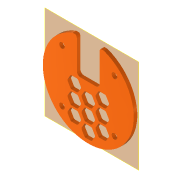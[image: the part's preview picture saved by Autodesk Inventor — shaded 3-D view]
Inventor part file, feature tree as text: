
AUTODESK INVENTOR PART (.ipt)
format: ipt  version: 2022 (Build 260153000, 153)  size: 285,696 bytes
history: native  units: mm
features: reference x6, extrude x3, sketch x3, plane x2, projected_geometry x2, other x2, hole x1, fillet x1, pattern_linear x1
ambient origin geometry x8: Origin, YZ Plane, XZ Plane, XY Plane, X Axis, Y Axis, Z Axis, Center Point
bodies: Volumenkörper1 (feature_tree)
feature tree (21):
  plane  "Arbeitsebene1"
  extrude  "Extrusion1"  Depth=4.0mm
  plane  "Arbeitsebene2"
  hole  "Bohrung1"  [1 undecoded]
  extrude  "Extrusion2"  Depth=2.0mm
  fillet  "Rundung1"  Radius=4.0mm
  extrude  "Extrusion3"  TaperAngle=0.0deg  [1 undecoded]
  pattern_linear  "Rechteckige Anordnung1"  Count1=3 Spacing1=8.0mm
  sketch  "Skizze1"  dims[d0=4.0mm d1=4.0mm]
  reference  "Referenz1"
  sketch  "Skizze2"  dims[d2=2.0mm d3=0.0mm]
  projected_geometry  "Projizierte Kontur1"
  reference  "Referenz2"
  reference  "Referenz3"
  reference  "Referenz4"
  reference  "Referenz5"
  reference  "Referenz6"
  sketch  "Skizze4"  dims[d4=3.2mm d5=6.0mm d6=4.0mm d7=2.0mm d8=90.0deg d9=8.0mm d10=20.594885mm d11=10.0mm d12=0.0mm d13=2.0mm d23=7.0mm d27=4.0mm d28=0.0mm d29=30.0mm d31=8.0mm d38=8.0mm d39=1.0mm d40=8.0mm d41=1.0mm d42=8.0mm d43=1.0mm d44=4.0mm d45=8.0mm d46=4.0mm d47=8.0mm d48=13.0mm d49=6.5mm]
  projected_geometry  "Projizierte Kontur2"
  other  "Assembly_Cube_SEEED_Xiao_Sense_Camera_v3.iam"
  other  "20_Cube_Insert_SEEED_Xiao_Sense_Camera:1"
note: 2 required parameter values undecoded (feature->parameter linkage not recoverable at this tier; creation-order binding heuristic only, values carry confidence <= 0.55)
